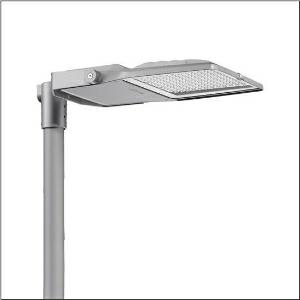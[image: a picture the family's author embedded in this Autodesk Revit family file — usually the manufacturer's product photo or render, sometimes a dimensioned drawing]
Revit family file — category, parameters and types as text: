
# Revit family: floodlight_fl_21_midi___pl52_5xa7785e2d3a_ba97
name_source: partatom
category: Lighting Fixtures
units: mm (PartAtom-declared; Revit-internal decimal feet)

## family parameters
Cut with Voids When Loaded = No
Host = Face
Light Source = No
Part Type = Normal
Room Calculation Point = No
Round Connector Dimension = Use Diameter
Shared = No

## types (1)
- --- (1 x LED, 26940 lm, 212.4 W, 3000K)
    Apparent Load = 212 VA
    CIE Flux Codes = 26 60 98 100 100
    Color Rendering = 70
    Color Temperature = 3000K
    Default Elevation = 1800 mm
    Description = Floodlight FL 21 midi, floodlight, primary light control with lens, of PMMA, primary optical cover: protective disc, of toughened safety glass, transparent, light distribution: PL52, light emission: direct distribution, installation type: surface-mounted, LED, High Power LED, rated luminous flux: 26.940lm, luminous efficacy: 127lm/W, light colour: 730, colour temperature: 3000K, control gear: Smart Interface (Zhaga), control: flexible luminous flux parameterisation, time-dependent luminous flux control, constant luminous flux control, overheat protection, pre-setting: logarithmic dimming characteristic, with terminal, 6-pole, mains connection: 220..240V, AC, 50/60Hz, start of lifetime: 212W, end of service life: 231W, reduction: 95W, luminaire housing, of diecast aluminium, powder-coated, Siteco® metallic grey (DB 702S), corrosivity category C5 mid according to DIN EN ISO 12944, suitable for swimming pools, chlorine-resistant, sealing non-destructively replaceable, please order mast flange separately, mast bracket, of steel, galvanised, powder-coated, Siteco® metallic grey (DB 702S), Smart Interface above, protection rating (complete): IP66, insulation class (complete): insulation class II (safety insulation), certification: CE, ENEC, VDE, protection symbol: D, impact resistance: IK08, permissible operating ambient temperature: -20..+40°C, permissible operating ambient temperature for outdoor applications: -40..+50°C, standard: DIN EN 12944, LABS conformity tested according to VDMA 24364:2018-05, packaging unit: 1 piece

Light Distribution: PL52
    Height = 76 mm
    Lamp = 1 x LED
    Lamp Light Flux = 26940 lm
    Lamp Power = 212.4 W
    Lamp count = 1
    Length = 657 mm
    Luminous efficacy = 127 lm/W
    Manufacturer = Siteco
    ModVariant = No
    Model = 5XA7785E2D3A
    Number of Poles = 1
    OnlyDefault = Yes
    Power Factor = 1
    Product Name = Floodlight FL 21 midi | PL52
    Product group = floodlight | pylon annexe
    ProductGroupID = 6200
    Protection Class = Protection class II
    Protection Degree = IP 66
    RLX_Detail_Level = 1
    RLX_Emergency_Light_Flux = 0 lm
    RLX_Emergency_Type = 0
    RLX_Emergency_Type_DB = No
    RlxData = <blob elided: 153913 chars, md5=546df6c2>
    Socket = socket
    Standby Power = 0 W
    System Light Flux = 26940 lm
    System Power = 212 W
    Type Comments = factory setting: luminous flux: 100 % | dim-lin: 254 | 710 mA
    Type Image = l_1007123.jpg
    URL = http://relux.com
    VarID = @adj_177630
    Voltage = 0 V
    Weight = 0.00 kg
    Width = 442 mm

## geometry (parser evidence)
native form markers: Blend x4, Sweep x14
no freeform markers — native parametric forms only
